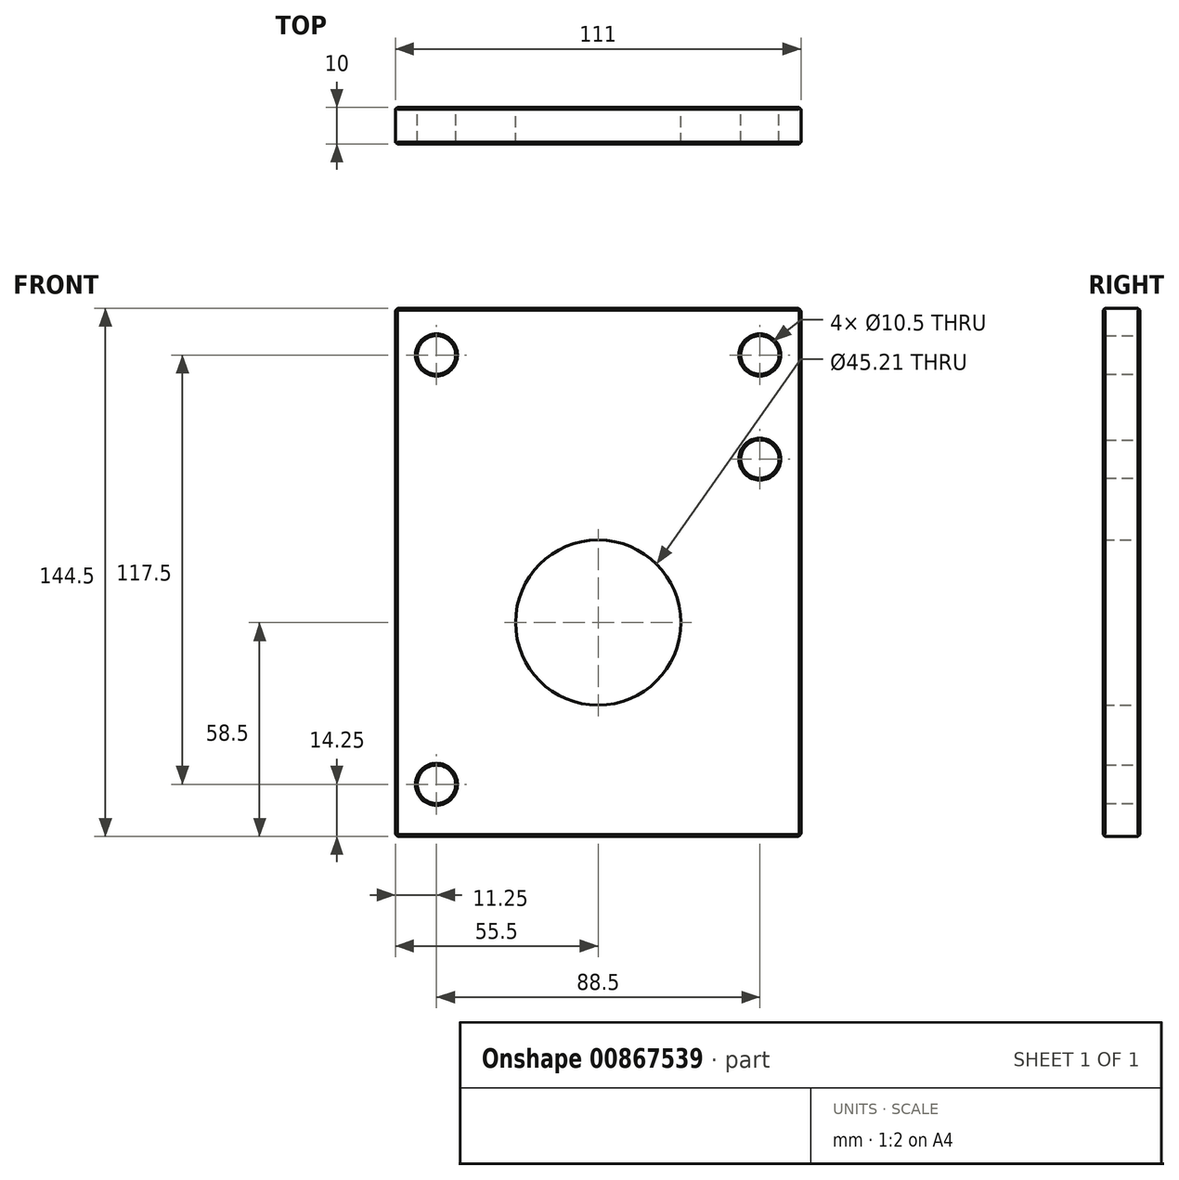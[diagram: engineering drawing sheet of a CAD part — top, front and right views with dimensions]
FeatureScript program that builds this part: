
annotation { "Feature Type Name" : "Feature", "Feature Type Description" : "" }
export const myFeature = defineFeature(function(context is Context, id is Id, definition is map)
    precondition{}
    {
        {
            var Q0;
            Q0=qCreatedBy(makeId("Front.planeOp"),FACE);
            var sketch = newSketch(context, id + "F0", { "sketchPlane" : qUnion([Q0])});
            skLineSegment(sketch, "E0.bottom", {"start": v(55.5, 72.25) * mm, "end": v(-55.5, 72.25) * mm});
            skLineSegment(sketch, "E0.top", {"start": v(55.5, -72.25) * mm, "end": v(-55.5, -72.25) * mm});
            skLineSegment(sketch, "E0.left", {"start": v(55.5, 72.25) * mm, "end": v(55.5, -72.25) * mm});
            skLineSegment(sketch, "E0.right", {"start": v(-55.5, 72.25) * mm, "end": v(-55.5, -72.25) * mm});
            skPoint(sketch, "E0.middle", {"position": v(0, 0) * mm});
            skCircle(sketch, "E1", {"center": v(-44.25, 59.5) * mm, "radius": 5.25 * mm});
            skCircle(sketch, "E2", {"center": v(44.25, 59.5) * mm, "radius": 5.25 * mm});
            skCircle(sketch, "E3", {"center": v(44.25, 31) * mm, "radius": 5.25 * mm});
            skCircle(sketch, "E4", {"center": v(-44.25, -58) * mm, "radius": 5.25 * mm});
            skCircle(sketch, "E5", {"center": v(0, -13.75) * mm, "radius": 22.6 * mm});
            skSolve(sketch);
        }
        {
            var Q0;
            Q0 = qSketchRegion(id + "F0", true);
            extrude(context, id + "F1", {"entities" : qUnion([Q0]), "depth" : 10 * mm, "offsetDistance" : 25 * mm});
        }
        {
            var Q0;
            Q0=makeQuery(id+"F1.opExtrude","CAP_EDGE",EDGE,{"disambiguationData":[OSD([sQuery(id+"F0.wireOp",EDGE,"E0.top")])],"isStart":false});
            var Q1;
            Q1=makeQuery(id+"F1.opExtrude","CAP_EDGE",EDGE,{"disambiguationData":[OSD([sQuery(id+"F0.wireOp",EDGE,"E0.right")])],"isStart":false});
            var Q2;
            Q2=makeQuery(id+"F1.opExtrude","CAP_EDGE",EDGE,{"disambiguationData":[OSD([sQuery(id+"F0.wireOp",EDGE,"E0.bottom")])],"isStart":false});
            var Q3;
            Q3=makeQuery(id+"F1.opExtrude","CAP_EDGE",EDGE,{"disambiguationData":[OSD([sQuery(id+"F0.wireOp",EDGE,"E0.left")])],"isStart":false});
            var Q4;
            Q4=makeQuery(id+"F1.opExtrude","CAP_EDGE",EDGE,{"disambiguationData":[OSD([sQuery(id+"F0.wireOp",EDGE,"E0.top")])],"isStart":true});
            var Q5;
            Q5=makeQuery(id+"F1.opExtrude","CAP_EDGE",EDGE,{"disambiguationData":[OSD([sQuery(id+"F0.wireOp",EDGE,"E0.left")])],"isStart":true});
            var Q6;
            Q6=makeQuery(id+"F1.opExtrude","CAP_EDGE",EDGE,{"disambiguationData":[OSD([sQuery(id+"F0.wireOp",EDGE,"E0.right")])],"isStart":true});
            var Q7;
            Q7=makeQuery(id+"F1.opExtrude","CAP_EDGE",EDGE,{"disambiguationData":[OSD([sQuery(id+"F0.wireOp",EDGE,"E0.bottom")])],"isStart":true});
            chamfer(context, id + "F2", {"entities" : qUnion([Q0, Q1, Q2, Q3, Q4, Q5, Q6, Q7]), "width" : .5 * mm, "tangentPropagation" : true});
        }
        {
            var Q0;
            Q0=makeQuery(id+"F1.opExtrude","SWEPT_EDGE",EDGE,{"disambiguationData":[OSD([sQuery(id+"F0.wireOp",EDGE,"E0.bottom"),sQuery(id+"F0.wireOp",EDGE,"E0.left")])]});
            var Q1;
            Q1=makeQuery(id+"F1.opExtrude","SWEPT_EDGE",EDGE,{"disambiguationData":[OSD([sQuery(id+"F0.wireOp",EDGE,"E0.top"),sQuery(id+"F0.wireOp",EDGE,"E0.left")])]});
            var Q2;
            Q2=makeQuery(id+"F1.opExtrude","SWEPT_EDGE",EDGE,{"disambiguationData":[OSD([sQuery(id+"F0.wireOp",EDGE,"E0.top"),sQuery(id+"F0.wireOp",EDGE,"E0.right")])]});
            var Q3;
            Q3=makeQuery(id+"F1.opExtrude","SWEPT_EDGE",EDGE,{"disambiguationData":[OSD([sQuery(id+"F0.wireOp",EDGE,"E0.bottom"),sQuery(id+"F0.wireOp",EDGE,"E0.right")])]});
            fillet(context, id + "F3", {"entities" : qUnion([Q0, Q1, Q2, Q3]), "radius" : 1 * mm, "tangentPropagation" : true, "allowEdgeOverflow" : false});
        }
        {
            var Q0;
            Q0=makeQuery(id+"F1.opExtrude","CAP_EDGE",EDGE,{"disambiguationData":[OSD([sQuery(id+"F0.wireOp",EDGE,"E1")])],"isStart":true});
            var Q1;
            Q1=makeQuery(id+"F1.opExtrude","CAP_EDGE",EDGE,{"disambiguationData":[OSD([sQuery(id+"F0.wireOp",EDGE,"E2")])],"isStart":true});
            var Q2;
            Q2=makeQuery(id+"F1.opExtrude","CAP_EDGE",EDGE,{"disambiguationData":[OSD([sQuery(id+"F0.wireOp",EDGE,"E3")])],"isStart":true});
            var Q3;
            Q3=makeQuery(id+"F1.opExtrude","CAP_EDGE",EDGE,{"disambiguationData":[OSD([sQuery(id+"F0.wireOp",EDGE,"E4")])],"isStart":true});
            var Q4;
            Q4=makeQuery(id+"F1.opExtrude","CAP_EDGE",EDGE,{"disambiguationData":[OSD([sQuery(id+"F0.wireOp",EDGE,"E1")])],"isStart":false});
            var Q5;
            Q5=makeQuery(id+"F1.opExtrude","CAP_EDGE",EDGE,{"disambiguationData":[OSD([sQuery(id+"F0.wireOp",EDGE,"E4")])],"isStart":false});
            var Q6;
            Q6=makeQuery(id+"F1.opExtrude","CAP_EDGE",EDGE,{"disambiguationData":[OSD([sQuery(id+"F0.wireOp",EDGE,"E3")])],"isStart":false});
            var Q7;
            Q7=makeQuery(id+"F1.opExtrude","CAP_EDGE",EDGE,{"disambiguationData":[OSD([sQuery(id+"F0.wireOp",EDGE,"E2")])],"isStart":false});
            chamfer(context, id + "F4", {"entities" : qUnion([Q0, Q1, Q2, Q3, Q4, Q5, Q6, Q7]), "width" : .5 * mm, "tangentPropagation" : true});
        }
    });
